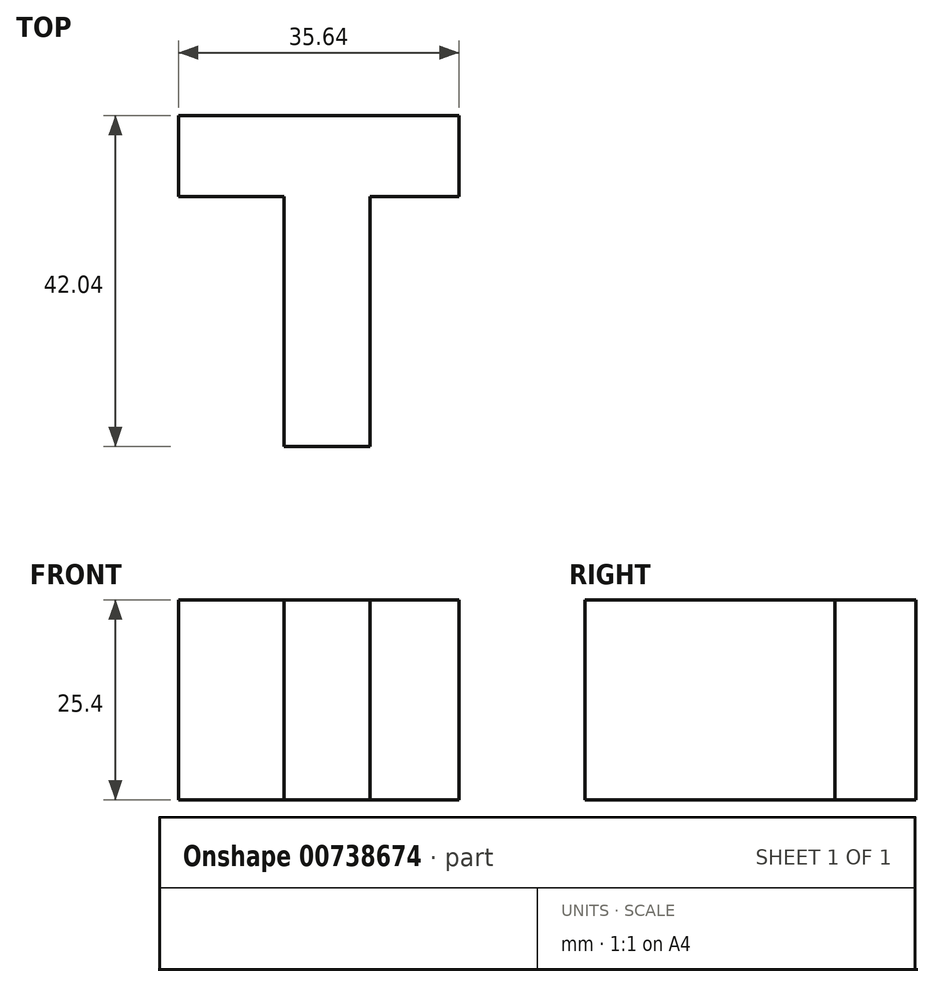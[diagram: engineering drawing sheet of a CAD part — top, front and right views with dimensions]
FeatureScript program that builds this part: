
annotation { "Feature Type Name" : "Feature", "Feature Type Description" : "" }
export const myFeature = defineFeature(function(context is Context, id is Id, definition is map)
    precondition{}
    {
        {
            var Q0;
            Q0=qCreatedBy(makeId("Top.planeOp"),FACE);
            var sketch = newSketch(context, id + "F0", { "sketchPlane" : qUnion([Q0])});
            skLineSegment(sketch, "E0", {"start": v(0, 0) * mm, "end": v(0, 31.75) * mm});
            skLineSegment(sketch, "E1", {"start": v(0, 0) * mm, "end": v(10.92, 0) * mm});
            skLineSegment(sketch, "E2", {"start": v(10.92, 0) * mm, "end": v(10.92, 31.75) * mm});
            skLineSegment(sketch, "E3", {"start": v(10.92, 31.75) * mm, "end": v(22.21, 31.75) * mm});
            skLineSegment(sketch, "E4", {"start": v(22.21, 31.75) * mm, "end": v(22.21, 42.04) * mm});
            skLineSegment(sketch, "E5", {"start": v(0, 42.04) * mm, "end": v(22.21, 42.04) * mm});
            skLineSegment(sketch, "E6", {"start": v(0, 31.75) * mm, "end": v(-13.43, 31.75) * mm});
            skLineSegment(sketch, "E7", {"start": v(-13.43, 31.75) * mm, "end": v(-13.43, 42.04) * mm});
            skLineSegment(sketch, "E8", {"start": v(-13.43, 42.04) * mm, "end": v(0, 42.04) * mm});
            skSolve(sketch);
        }
        {
            var Q0;
            Q0 = qSketchRegion(id + "F0", true);
            extrude(context, id + "F1", {"entities" : qUnion([Q0]), "oppositeDirection" : true, "depth" : 25.4 * mm, "offsetDistance" : 25.4 * mm});
        }
    });
